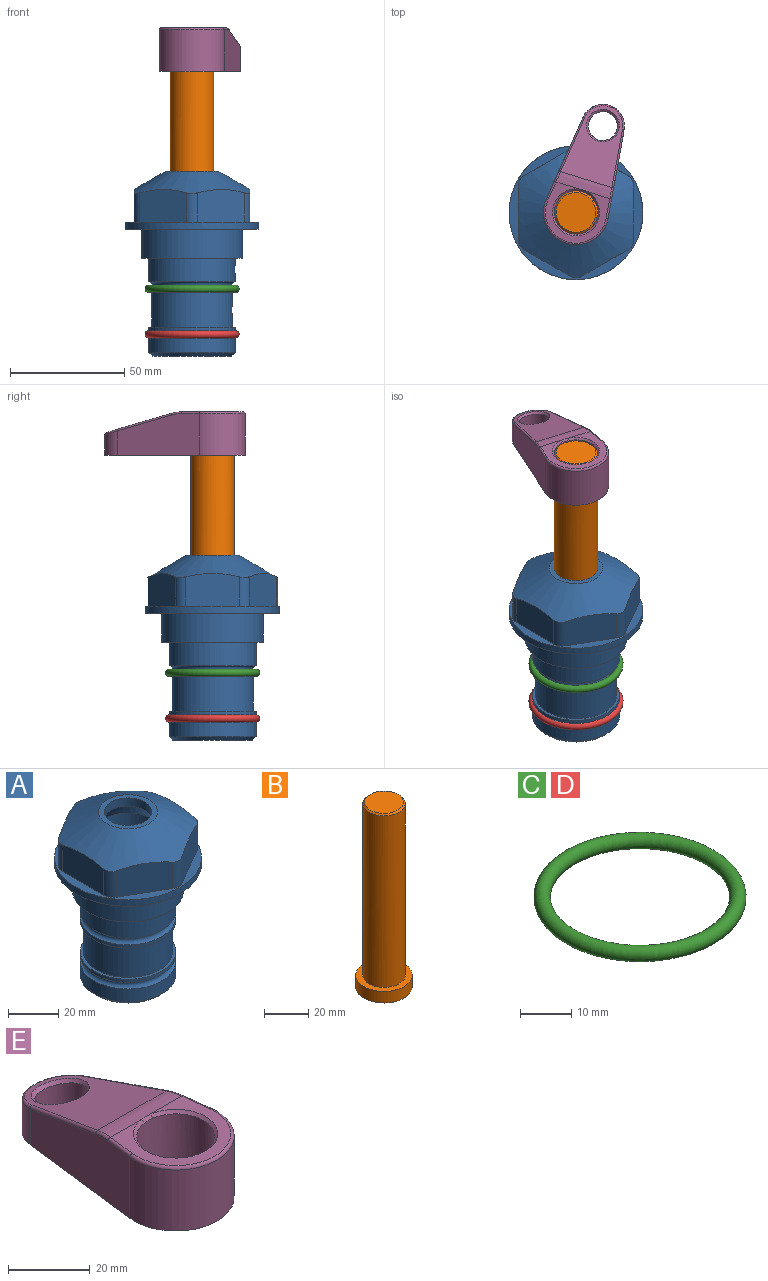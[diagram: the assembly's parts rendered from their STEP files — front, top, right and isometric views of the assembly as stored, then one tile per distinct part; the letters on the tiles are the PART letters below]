
ASSEMBLY  parts=5 mates=4
PART A: 36 faces, bbox 58.7x58.7x81 mm
  f0: cylinder r=17.78mm len=35.56mm, axis (0,0,1), area 1670.8mm2, adj f23,f24,f31
  f1: cylinder r=19.05mm len=38.1mm, axis (0,0,1), area 1191.9mm2, adj f26,f27,f30
  f2: plane 58.66x58.66mm, normal (0,0,-1), area 1150.6mm2, adj f3,f28
  f3: cylinder r=29.33mm len=58.66mm, axis (0,0,-1), area 585.1mm2, adj f2,f4
  f4: plane 58.66x58.66mm, normal (0,0,1), area 475.9mm2, adj f3,f5,f6,f7,f8,f9,f10,f11
  f5: plane 20.32x14.34mm, normal (-0.5,0.87,0), area 324.4mm2, adj f4,f15,f16,f17
  f6: plane 20.32x14.34mm, normal (0.5,0.87,0), area 324.4mm2, adj f4,f14,f15,f17
  f7: plane 23.48x14.34mm, normal (1,0,0), area 324.4mm2, adj f4,f13,f14,f17
  f8: plane 20.32x14.34mm, normal (0.5,-0.87,0), area 324.4mm2, adj f4,f12,f13,f17
  f9: plane 20.32x14.34mm, normal (-0.5,-0.87,0), area 324.4mm2, adj f4,f11,f12,f17
  f10: plane 23.48x14.34mm, normal (-1,0,0), area 324.4mm2, adj f4,f11,f16,f17
  f11: cylinder r=5.08mm len=12.85mm, axis (0,0,-1), area 67.2mm2, adj f4,f9,f10,f17
  f12: cylinder r=5.08mm len=12.85mm, axis (0,0,-1), area 67.2mm2, adj f4,f8,f9,f17
  f13: cylinder r=5.08mm len=12.85mm, axis (0,0,-1), area 67.2mm2, adj f4,f7,f8,f17
  f14: cylinder r=5.08mm len=12.85mm, axis (0,0,-1), area 67.2mm2, adj f4,f6,f7,f17
  f15: cylinder r=5.08mm len=12.85mm, axis (0,0,-1), area 67.2mm2, adj f4,f5,f6,f17
  f16: cylinder r=5.08mm len=12.85mm, axis (0,0,-1), area 67.2mm2, adj f4,f5,f10,f17
  f17: cone r=11.73mm half-angle=60deg, axis (0,0,-1), area 2071.8mm2, adj f5,f6,f7,f8,f9,f10,f11,f12
  f18: plane 23.46x23.46mm, normal (0,0,1), area 147.4mm2, adj f17,f35
  f19: plane 34.93x34.93mm, normal (0,0,-1), area 958mm2, adj f29
  f20: cylinder r=19.05mm len=38.1mm, axis (0,0,1), area 760.1mm2, adj f21,f29
  f21: torus R=19.05mm, axis (0,0,1), area 565.3mm2, adj f20,f22
  f22: cylinder r=19.05mm len=38.1mm, axis (0,0,1), area 190mm2, adj f21,f23
  f23: plane 38.1x38.1mm, normal (0,0,1), area 146.9mm2, adj f0,f22
  f24: plane 38.1x38.1mm, normal (0,0,-1), area 146.9mm2, adj f0,f25
  f25: cylinder r=19.05mm len=38.1mm, axis (0,0,1), area 190mm2, adj f24,f26
  f26: torus R=19.05mm, axis (0,0,1), area 565.3mm2, adj f1,f25
  f27: plane 44.45x44.45mm, normal (0,0,-1), area 411.7mm2, adj f1,f28
  f28: cylinder r=22.23mm len=44.45mm, axis (0,0,1), area 1773.5mm2, adj f2,f27
  f29: cone r=19.05mm half-angle=45deg, axis (0,0,1), area 257.5mm2, adj f19,f20
  f30: cylinder r=3.17mm len=6.75mm, axis (-1,0,0), area 128mm2, adj f1,f33
  f31: cylinder r=3.17mm len=6.35mm, axis (-1,0,0), area 102.5mm2, adj f0,f33
  f32: plane 25.4x25.4mm, normal (0,0,1), area 506.7mm2, adj f33
  f33: cylinder r=12.7mm len=66.42mm, axis (0,0,-1), area 5236.2mm2, adj f30,f31,f32,f34
  f34: cone r=9.53mm half-angle=30deg, axis (0,0,-1), area 443.4mm2, adj f33,f35
  f35: cylinder r=9.53mm len=19.05mm, axis (0,0,-1), area 240.9mm2, adj f18,f34
PART B: 6 faces, bbox 25.4x25.4x101.6 mm
  f0: plane 17.46x17.46mm, normal (0,0,1), area 239.5mm2, adj f5
  f1: plane 25.4x25.4mm, normal (0,0,-1), area 506.7mm2, adj f2
  f2: cylinder r=12.7mm len=25.4mm, axis (0,0,1), area 506.7mm2, adj f1,f3
  f3: plane 25.4x25.4mm, normal (0,0,1), area 221.7mm2, adj f2,f4
  f4: cylinder r=9.53mm len=94.46mm, axis (0,0,1), area 5653mm2, adj f3,f5
  f5: cone r=8.73mm half-angle=45deg, axis (0,0,-1), area 64.4mm2, adj f0,f4
PART C: 1 faces, bbox 44.7x44.7x3.2 mm
  f0: torus R=19.05mm, axis (0,0,1), area 1193.9mm2
PART D: same geometry as C
PART E: 31 faces, bbox 31.7x65.5x19.8 mm
  f0: plane 39.12x18.26mm, normal (0.99,0.12,0), area 612.2mm2, adj f1,f4,f7,f11,f13,f15
  f1: cylinder r=9.53mm len=18.91mm, axis (0,0,-1), area 296.1mm2, adj f0,f2,f7,f17
  f2: plane 39.12x18.26mm, normal (-0.99,0.12,0), area 612.2mm2, adj f1,f4,f7,f12,f14,f16
  f3: cylinder r=6.35mm len=12.7mm, axis (0,0,-1), area 362.4mm2, adj f7,f18
  f4: cylinder r=14.29mm len=28.58mm, axis (0,0,-1), area 882.2mm2, adj f0,f2,f7,f10
  f5: cylinder r=9.53mm len=19.05mm, axis (0,0,-1), area 1092.6mm2, adj f7,f19,f20
  f6: plane 26.99x23.69mm, normal (0,0,1), area 216.2mm2, adj f9,f10,f11,f12,f19
  f7: plane 63.5x28.58mm, normal (0,0,-1), area 661.8mm2, adj f0,f1,f2,f3,f4,f5,f22,f23
  f8: plane 33.52x23.6mm, normal (0,0.26,0.97), area 486mm2, adj f9,f15,f16,f17,f18
  f9: cylinder r=19.05mm len=24.72mm, axis (1,0,0), area 120.4mm2, adj f6,f8,f13,f14,f20
  f10: torus R=13.49mm, axis (0,0,1), area 59mm2, adj f4,f6,f11,f12
  f11: cylinder r=0.79mm len=8.67mm, axis (0.12,-0.99,0), area 10.8mm2, adj f0,f6,f10,f13
  f12: cylinder r=0.79mm len=8.67mm, axis (0.12,0.99,0), area 10.8mm2, adj f2,f6,f10,f14
  f13: bspline ~4.95x1.42mm, area 6.1mm2, adj f0,f9,f11,f15
  f14: bspline ~4.95x1.42mm, area 6.1mm2, adj f2,f9,f12,f16
  f15: cylinder r=0.79mm len=25.95mm, axis (0.12,-0.96,0.26), area 32.9mm2, adj f0,f8,f13,f17
  f16: cylinder r=0.79mm len=25.95mm, axis (0.12,0.96,-0.26), area 32.9mm2, adj f2,f8,f14,f17
  f17: bspline ~18.91x8.38mm, area 30mm2, adj f1,f8,f15,f16
  f18: bspline ~14.29x14.29mm, area 48.3mm2, adj f3,f8
  f19: cone r=9.53mm half-angle=45deg, axis (0,0,1), area 66.5mm2, adj f5,f6,f20
  f20: bspline ~3.22x0.96mm, area 3.5mm2, adj f5,f9,f19
  f21: plane 2.75x2.72mm, normal (0,0,-1), area 2.9mm2, adj f23,f25,f28
  f22: plane 23.05x15.88mm, normal (-0.99,-0.12,0), area 323.6mm2, adj f7,f25,f26,f27,f28,f29
  f23: plane 23.05x15.88mm, normal (0.99,-0.12,0), area 323.6mm2, adj f7,f21,f25,f27,f28,f30
  f24: cylinder r=9.53mm len=10.69mm, axis (0,0,-1), area 114.7mm2, adj f7,f27,f29,f30
  f25: cylinder r=12.7mm len=20.59mm, axis (0,0,-1), area 381.1mm2, adj f7,f21,f22,f23,f26,f28
  f26: plane 2.75x2.72mm, normal (0,0,-1), area 2.9mm2, adj f22,f25,f28
  f27: plane 19.72x18.37mm, normal (0,-0.26,-0.97), area 291.8mm2, adj f22,f23,f24,f28,f29,f30
  f28: cylinder r=15.88mm len=19.92mm, axis (1,0,0), area 54.8mm2, adj f21,f22,f23,f25,f26,f27
  f29: cylinder r=1.59mm len=11mm, axis (0,0,-1), area 34.7mm2, adj f7,f22,f24,f27
  f30: cylinder r=1.59mm len=11mm, axis (0,0,-1), area 34.7mm2, adj f7,f23,f24,f27
PLACE A at identity fixed
PLACE B rot(axis=(0,0,-1),17.2deg) t=(0,0,24.06)mm
PLACE C t=(0,0,-1.59)mm
PLACE D t=(0,0,-21.59)mm
PLACE E rot(axis=(0,0,-1),17.2deg) t=(0,0,24.86)mm
MATE cylindrical B.f2 <-> A.f0  axis (0,0,-1) through (0,0,-14.04)mm
MATE fastened E.f4 <-> B.f2  axis (0,0,1) through (0,0,87.56)mm
MATE fastened D.f0 <-> A.f0  axis (0,0,1) through (0,0,-46.1)mm
MATE fastened C.f0 <-> A.f0  axis (0,0,1) through (0,0,-26.1)mm
